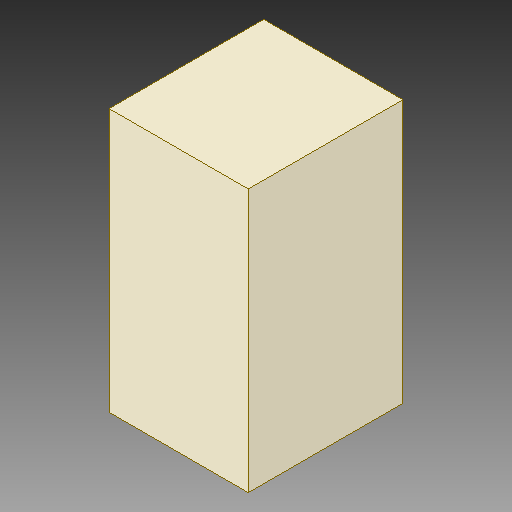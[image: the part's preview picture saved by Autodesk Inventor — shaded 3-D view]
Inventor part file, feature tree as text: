
AUTODESK INVENTOR PART (.ipt)
format: ipt  version: 2018 (Build 220112000, 112)  size: 81,920 bytes
history: native  units: in
note: dims shown in document units (in); Inventor stores cm internally (conversion verified against a paired STEP export)
features: other x1, extrude x1
ambient origin geometry x8: Origin, YZ Plane, XZ Plane, XY Plane, X Axis, Y Axis, Z Axis, Center Point
bodies: Solid1 (feature_tree)
feature tree (2):
  other  "CHIPLED_0603, CHIPLED_0603_83"
  extrude  "Extrusion1"  Depth=0.0394in TaperAngle=0.0deg
